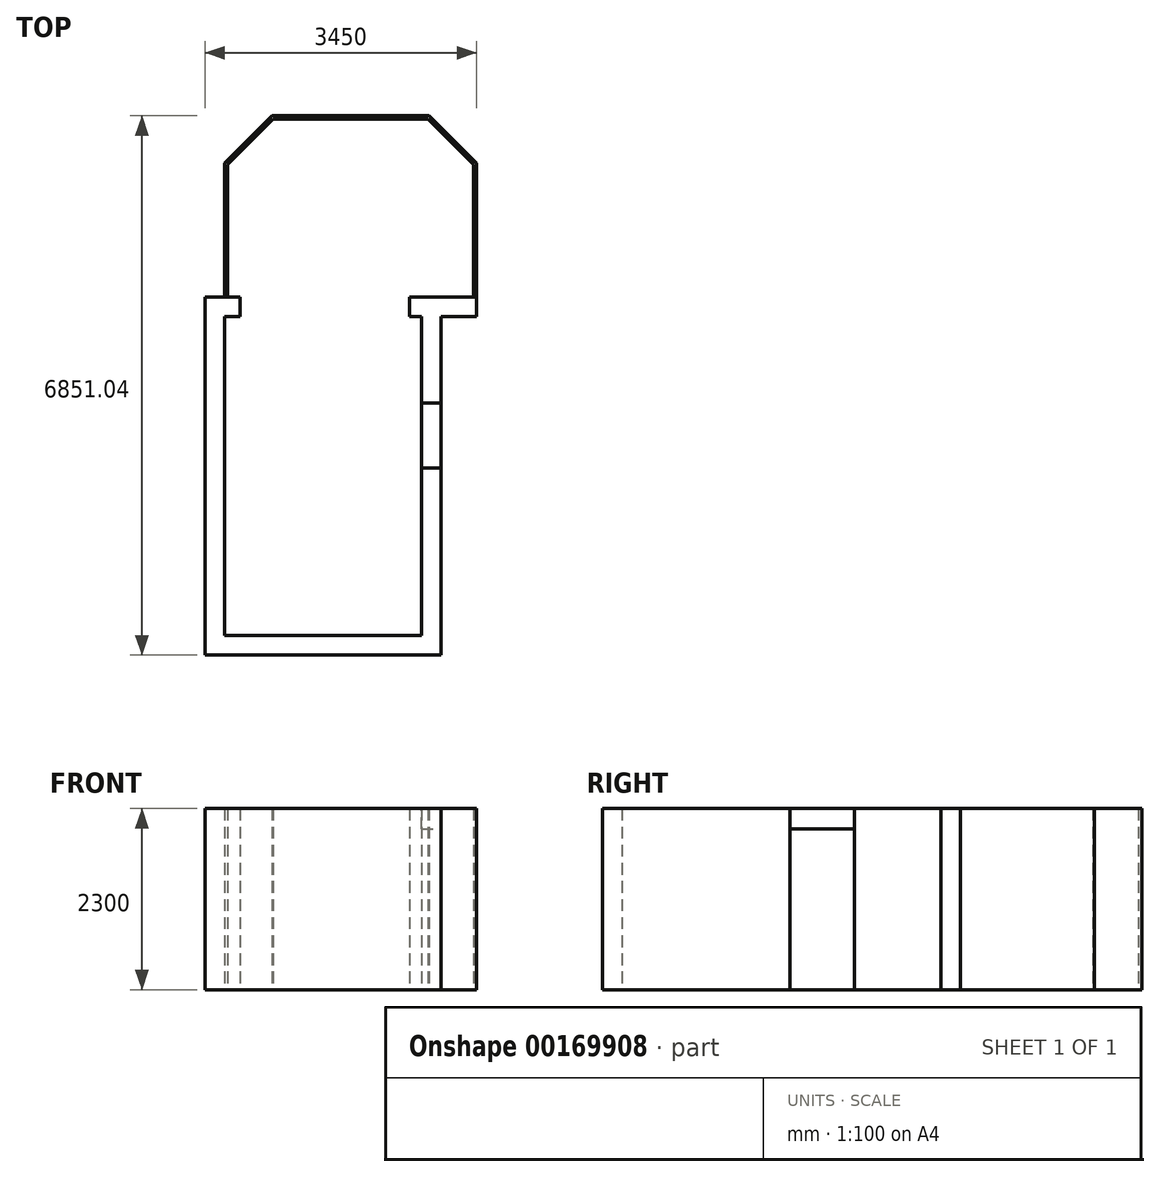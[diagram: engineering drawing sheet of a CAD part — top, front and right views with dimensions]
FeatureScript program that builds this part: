
annotation { "Feature Type Name" : "Feature", "Feature Type Description" : "" }
export const myFeature = defineFeature(function(context is Context, id is Id, definition is map)
    precondition{}
    {
        {
            var Q0;
            Q0=qCreatedBy(makeId("Top.planeOp"),FACE);
            var sketch = newSketch(context, id + "F0", { "sketchPlane" : qUnion([Q0])});
            skLineSegment(sketch, "E0.bottom", {"start": v(-1250, 2025) * mm, "end": v(1250, 2025) * mm});
            skLineSegment(sketch, "E0.top", {"start": v(-1250, -2025) * mm, "end": v(1250, -2025) * mm});
            skLineSegment(sketch, "E0.left", {"start": v(-1250, 2025) * mm, "end": v(-1250, -2025) * mm});
            skLineSegment(sketch, "E0.right", {"start": v(1250, 2025) * mm, "end": v(1250, -2025) * mm});
            skPoint(sketch, "E0.middle", {"position": v(0, 0) * mm});
            skLineSegment(sketch, "E1.0", {"start": v(-1500, 2275) * mm, "end": v(1500, 2275) * mm});
            skLineSegment(sketch, "E1.1", {"start": v(-1500, 2275) * mm, "end": v(-1500, -2275) * mm});
            skLineSegment(sketch, "E1.2", {"start": v(-1500, -2275) * mm, "end": v(1500, -2275) * mm});
            skLineSegment(sketch, "E1.3", {"start": v(1500, 2025) * mm, "end": v(1500, -2275) * mm});
            skLineSegment(sketch, "E2", {"start": v(-1050, 2025) * mm, "end": v(-1050, 2275) * mm});
            skLineSegment(sketch, "E3", {"start": v(1100, 2275) * mm, "end": v(1100, 2025) * mm});
            skLineSegment(sketch, "E4", {"start": v(1250, 925) * mm, "end": v(1500, 925) * mm});
            skLineSegment(sketch, "E5", {"start": v(1250, 105) * mm, "end": v(1500, 105) * mm});
            skLineSegment(sketch, "E6", {"start": v(1250, 105) * mm, "end": v(430, 105) * mm});
            skArc(sketch, "E7", {"start": v(1250, 925) * mm, "mid": v(670.17, 684.83) * mm, "end": v(430, 105) * mm});
            skArc(sketch, "E8", {"start": v(280, 2025) * mm, "mid": v(520.17, 1445.17) * mm, "end": v(1100, 1205) * mm});
            skLineSegment(sketch, "E9", {"start": v(1100, 2025) * mm, "end": v(1100, 1205) * mm});
            skLineSegment(sketch, "E10", {"start": v(-1250, 2275) * mm, "end": v(-1250, 3975) * mm});
            skLineSegment(sketch, "E11", {"start": v(-1250, 3975) * mm, "end": v(-648.96, 4576.04) * mm});
            skLineSegment(sketch, "E12", {"start": v(-648.96, 4576.04) * mm, "end": v(1348.96, 4576.04) * mm});
            skLineSegment(sketch, "E13", {"start": v(1348.96, 4576.04) * mm, "end": v(1950, 3975) * mm});
            skLineSegment(sketch, "E14", {"start": v(1950, 3975) * mm, "end": v(1950, 2275) * mm});
            skLineSegment(sketch, "E15", {"start": v(1500, 2275) * mm, "end": v(1950, 2275) * mm});
            skLineSegment(sketch, "E16", {"start": v(350, 2275) * mm, "end": v(350, 4576.04) * mm, "construction": true});
            skLineSegment(sketch, "E17.0", {"start": v(1910, 3958.43) * mm, "end": v(1910, 2275) * mm});
            skLineSegment(sketch, "E17.1", {"start": v(-1210, 2275) * mm, "end": v(-1210, 3958.43) * mm});
            skLineSegment(sketch, "E17.2", {"start": v(-1210, 3958.43) * mm, "end": v(-632.4, 4536.04) * mm});
            skLineSegment(sketch, "E17.3", {"start": v(-632.4, 4536.04) * mm, "end": v(1332.4, 4536.04) * mm});
            skLineSegment(sketch, "E17.4", {"start": v(1332.4, 4536.04) * mm, "end": v(1910, 3958.43) * mm});
            skLineSegment(sketch, "E18.bottom", {"start": v(1950, 2275) * mm, "end": v(1500, 2275) * mm});
            skLineSegment(sketch, "E18.top", {"start": v(1950, 2025) * mm, "end": v(1500, 2025) * mm});
            skLineSegment(sketch, "E18.left", {"start": v(1950, 2275) * mm, "end": v(1950, 2025) * mm});
            skSolve(sketch);
        }
        {
            var Q0;
            {var subQ9=sQuery(id+"F0.wireOp",EDGE,"E0.top");Q0=makeQuery(id+"F0.imprint","IMPRINT",FACE,{"disambiguationData":[TD([[makeQuery(id+"F0.imprint","IMPRINT",EDGE,{"derivedFrom":subQ9}),-1.0]])]});}
            var Q1;
            {var subQ4=sQuery(id+"F0.wireOp",EDGE,"E3");Q1=makeQuery(id+"F0.imprint","IMPRINT",FACE,{"disambiguationData":[TD([[makeQuery(id+"F0.imprint","IMPRINT",EDGE,{"derivedFrom":subQ4}),1.0]])]});}
            extrude(context, id + "F1", {"entities" : qUnion([Q0, Q1]), "depth" : 2300 * mm, "offsetDistance" : 25 * mm});
        }
        {
            var Q0;
            {var subQ0=sQuery(id+"F0.wireOp",EDGE,"E1.3");Q0=makeQuery(id+"F1.opExtrude","SWEPT_FACE",FACE,{"disambiguationData":[OSD([subQ0]),TDD([makeQuery(id+"F0.imprint","IMPRINT",EDGE,{"disambiguationData":[TD([[makeQuery(id+"F0.imprint","INTERSECT",VERTEX,{"derivedFrom":[subQ0,sQuery(id+"F0.wireOp",EDGE,"E4")]}),1.0]])],"derivedFrom":subQ0})])]});}
            var sketch = newSketch(context, id + "F2", { "sketchPlane" : qUnion([Q0])});
            skLineSegment(sketch, "E19.bottom", {"start": v(925, 2300) * mm, "end": v(105, 2300) * mm});
            skLineSegment(sketch, "E19.top", {"start": v(925, 2040) * mm, "end": v(105, 2040) * mm});
            skLineSegment(sketch, "E19.left", {"start": v(925, 2300) * mm, "end": v(925, 2040) * mm});
            skLineSegment(sketch, "E19.right", {"start": v(105, 2300) * mm, "end": v(105, 2040) * mm});
            skSolve(sketch);
        }
        {
            var Q0;
            Q0=makeQuery(id+"F2.imprint","IMPRINT",FACE,{"disambiguationData":[TD([[makeQuery(id+"F2.imprint","IMPRINT",EDGE,{"derivedFrom":sQuery(id+"F2.wireOp",EDGE,"E19.bottom")}),1.0]])]});
            var Q1;
            {var subQ0=sQuery(id+"F0.wireOp",EDGE,"E0.right");Q1=makeQuery(id+"F1.opExtrude","SWEPT_FACE",FACE,{"disambiguationData":[OSD([subQ0]),TDD([makeQuery(id+"F0.imprint","IMPRINT",EDGE,{"disambiguationData":[TD([[makeQuery(id+"F0.imprint","INTERSECT",VERTEX,{"derivedFrom":[sQuery(id+"F0.wireOp",EDGE,"E0.top"),subQ0]}),1.0]])],"derivedFrom":subQ0})])]});}
            extrude(context, id + "F3", {"entities" : qUnion([Q0]), "endBound" : BoundingType.UP_TO_SURFACE, "oppositeDirection" : true, "depth" : 25 * mm, "endBoundEntityFace" : qUnion([Q1]), "offsetDistance" : 25 * mm});
        }
        {
            var Q0;
            {var subQ3=sQuery(id+"F0.wireOp",EDGE,"E10");Q0=makeQuery(id+"F0.imprint","IMPRINT",FACE,{"disambiguationData":[TD([[makeQuery(id+"F0.imprint","IMPRINT",EDGE,{"derivedFrom":subQ3}),-1.0]])]});}
            var Q1;
            Q1=sQuery(id+"F0.wireOp",EDGE,"E14");
            var Q2;
            Q2=sQuery(id+"F0.wireOp",EDGE,"E13");
            var Q3;
            Q3=sQuery(id+"F0.wireOp",EDGE,"E11");
            var Q4;
            Q4=sQuery(id+"F0.wireOp",EDGE,"E10");
            extrude(context, id + "F4", {"entities" : qUnion([Q0]), "surfaceEntities" : qUnion([Q1, Q2, Q3, Q4]), "depth" : 2300 * mm, "offsetDistance" : 25 * mm});
        }
    });
